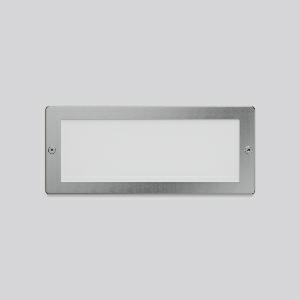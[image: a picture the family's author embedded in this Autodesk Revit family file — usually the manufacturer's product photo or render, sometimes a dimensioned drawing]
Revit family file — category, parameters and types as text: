
# Revit family: brick_steps_641307_000_c9fd
name_source: partatom
category: Lighting Fixtures
units: mm (PartAtom-declared; Revit-internal decimal feet)

## family parameters
Cut with Voids When Loaded = No
Host = Face
Light Source = No
Part Type = Normal
Room Calculation Point = No
Round Connector Dimension = Use Diameter
Shared = No

## types (1)
- BRICK STEPS (1 x LED Modul 830, 200 lm, 3000)
    Apparent Load = 6 VA
    CIE Flux Codes = 13 37 67 50 100
    Color Rendering = 80
    Color Temperature = 3000
    Default Elevation = 1800 mm
    Description = Series: BRICK STEPS
Robust LED wall and step luminaires. Housing: die-cast aluminium, powder-coated. Shock resistant plastic (polycarbonate) cover, opal, with stainless steel frame. Driver integrated. With second cable entry for loop through. Recommended accessory: recessed support. 
Colour: stainless steel
Length: 236 mm
Width: 100 mm
Height: 5 mm
Lamp: LED
System power: 6 W
Rated luminous flux: 200 lm
Luminous efficiency: 33 lm/W
Control gear: Regulated power supply
Protection class: I
Type of protection: IP 66
    Height = 5 mm  [stored 0.0164042 ft]
    Lamp = 1 x LED Modul 830
    Lamp Light Flux = 200 lm
    Lamp count = 1
    Length = 236 mm
    Lifetime = 50000 h
    Luminous efficacy = 33 lm/W
    Manufacturer = RZB
    ModVariant = No
    Model = 641307.000
    Mounting Place = Wall
    Mounting Type = Recessed
    Number of Poles = 1
    OnlyDefault = Yes
    Power Factor = 1
    Product Name = BRICK STEPS
    Product group = Recessed wall luminaires
    ProductGroupID = 2004
    Protection Class = Protection class I
    Protection Degree = IP 66
    RLX_Detail_Level = 1
    RLX_Emergency_Light_Flux = 0 lm
    RLX_Emergency_Type = 0
    RLX_Emergency_Type_DB = No
    RlxData = <blob elided: 35693 chars, md5=099d826f>
    Socket = socket
    Standby Power = 0 W
    System Light Flux = 200 lm
    System Power = 6 W
    Type Comments = Product without accessories
    Type Image = 641307.000.jpg
    URL = http://relux.com
    VarID = ---
    Voltage = 230 V
    Voltage Range = 220-240 V
    Weight = 0.00 kg
    Width = 100 mm  [stored 0.328084 ft]

note: [stored X ft] marks values corroborated as IEEE doubles in the binary element streams (Revit-internal decimal feet)

## geometry (parser evidence)
native form markers: Blend x4, Sweep x13
no freeform markers — native parametric forms only
